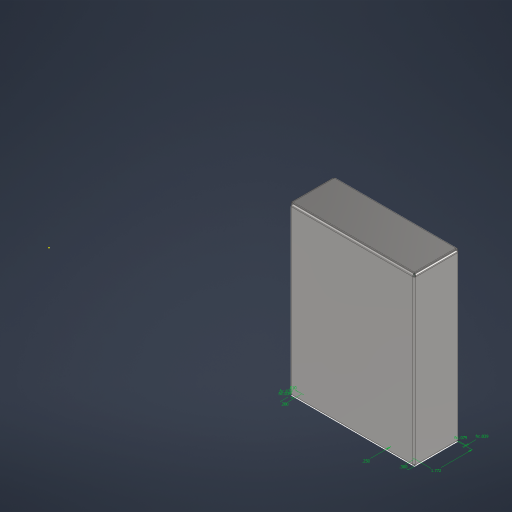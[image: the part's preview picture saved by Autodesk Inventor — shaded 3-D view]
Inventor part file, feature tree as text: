
AUTODESK INVENTOR PART (.ipt)
format: ipt  version: 2024.2 (Build 282272000, 272)  size: 611,840 bytes
history: native  units: in
note: dims shown in document units (in); Inventor stores cm internally (conversion verified against a paired STEP export)
features: sheet_metal_op x12, other x7, sketch x3, plane x2
ambient origin geometry x8: Origin, YZ Plane, XZ Plane, XY Plane, X Axis, Y Axis, Z Axis, Center Point
bodies: Solid2 (feature_tree), Solid3 (feature_tree), Solid1 (feature_tree)
feature tree (24):
  other  "HV servo drive v1_PCB.ipt"
  plane  "Work Plane1"
  sketch  "Sketch1"  dims[d0=0.3937in]
  plane  "Work Plane2"
  sheet_metal_op  "Contour Flange1"
  sheet_metal_op  "Flange1"
  sheet_metal_op  "Contour Flange2"
  sheet_metal_op  "Flange2"
  other  "Solid1::HV servo drive v1_PCB.ipt"
  other  "TaggingFeature1"
  other  "Plate1"
  sheet_metal_op  "Bend1"
  sheet_metal_op  "Corner1"
  sketch  "Sketch2"  dims[d1=0.0625in]
  other  "Plate2"
  sheet_metal_op  "Bend2"
  sheet_metal_op  "Corner2"
  other  "Plate3"
  sheet_metal_op  "Bend3"
  sheet_metal_op  "Corner3"
  sketch  "Sketch3"  dims[d2=0.3in d3=0.25in d4=0.2in d7=0.0625in d8=0.0394in d9=0.0394in d10=0.0197in d11=0.0787in d12=0.0394in d13=8.0in d14=0.0394in d15=0.039in d16=0.1575in d17=0.0394in d18=0.0394in d20=1.7717in d21=0.01in d22=0.0394in d23=0.0197in d24=0.0787in d25=0.0394in d26=0.3in d27=90.0deg d28=0.0394in d29=0.1575in d30=0.0394in d31=0.0394in d32=0.0394in d33=0.0394in d34=0.0787in d35=0.0787in d36=0.0394in d37=0.0394in d38=0.0197in d39=0.0787in d40=0.0394in d41=8.0in d42=0.0394in d43=0.039in d44=0.1575in d45=0.0394in d46=0.0394in d47=0.0394in d48=0.0197in d49=0.0787in d50=0.0394in d51=0.3in d52=90.0deg d53=0.0394in d54=0.0in d55=0.1575in d56=0.0394in d57=0.0394in]
  other  "Plate4"
  sheet_metal_op  "Bend4"
  sheet_metal_op  "Corner4"
